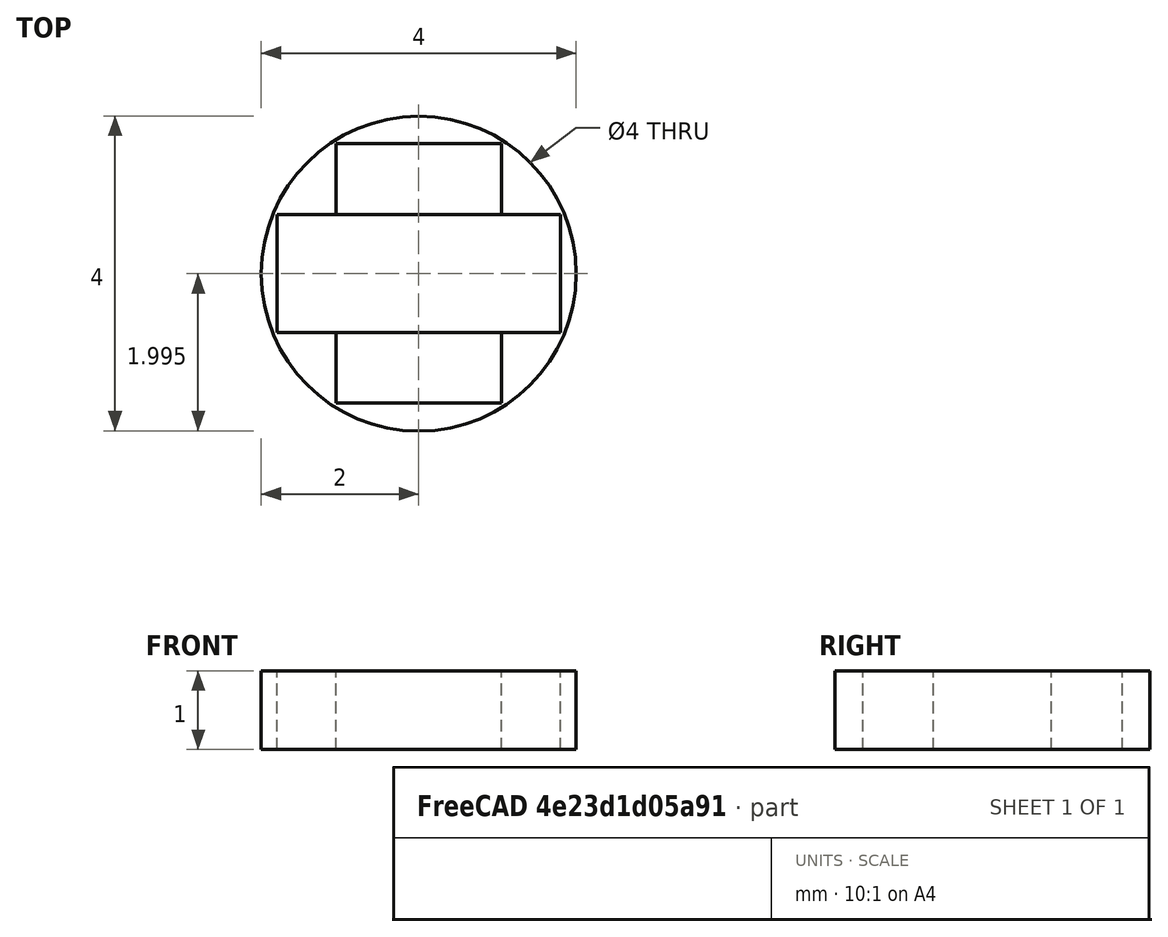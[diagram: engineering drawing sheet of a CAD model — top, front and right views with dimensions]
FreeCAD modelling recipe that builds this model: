
FCSTD DOCUMENT  (FreeCAD 0.17R13541 (Git))
Label: NOSE-PLANE
License: All rights reserved
LicenseURL: http://en.wikipedia.org/wiki/All_rights_reserved
objects: Drawing::FeatureViewPython×7, Part::Extrusion×2, Sketcher::SketchObject×1, Part::Feature×1, Drawing::FeatureViewPart×1, Drawing::FeaturePage×1
note: 4 computed .brp shape members not serialized (recipe doc carries the construction recipe); baked Part::Feature solids carry a one-line shape summary decoded from their .brp

FEATURE [Sketcher::SketchObject] Sketch
  sketch-geometry (11):
    g0: LineSegment StartX=-1.8 StartY=0.75 StartZ=0 EndX=1.8 EndY=0.75 EndZ=0
    g1: LineSegment StartX=1.8 StartY=0.75 StartZ=0 EndX=1.8 EndY=-0.75 EndZ=0
    g2: LineSegment StartX=1.8 StartY=-0.75 StartZ=0 EndX=-1.8 EndY=-0.75 EndZ=0
    g3: LineSegment StartX=-1.8 StartY=-0.75 StartZ=0 EndX=-1.8 EndY=0.75 EndZ=0
    g4: LineSegment StartX=-1.05 StartY=0.75 StartZ=0 EndX=-1.05 EndY=1.65 EndZ=0
    g5: LineSegment StartX=-1.05 StartY=1.65 StartZ=0 EndX=1.05 EndY=1.65 EndZ=0
    g6: LineSegment StartX=1.05 StartY=1.65 StartZ=0 EndX=1.05 EndY=0.75 EndZ=0
    g7: Circle CenterX=0.000107 CenterY=-0.004869 CenterZ=0 NormalX=0 NormalY=0 NormalZ=1 AngleXU=0 Radius=2
    g8: LineSegment StartX=-1.05 StartY=-0.75 StartZ=0 EndX=-1.05 EndY=-1.65 EndZ=0
    g9: LineSegment StartX=-1.05 StartY=-1.65 StartZ=0 EndX=1.05 EndY=-1.65 EndZ=0
    g10: LineSegment StartX=1.05 StartY=-1.65 StartZ=0 EndX=1.05 EndY=-0.75 EndZ=0
  constraints (33):
    c: Horizontal(g0)
    c: Coincident(g1,g0)
    c: Vertical(g1)
    c: Coincident(g2,g1)
    c: Horizontal(g2)
    c: Coincident(g3,g2)
    c: Coincident(g3,g0)
    c: Vertical(g3)
    c: Distance(g0) = 3.6
    c: Distance(g1) = 1.5
    c: Symmetric(g0,g0,g-2)
    c: Symmetric(g0,g1,g-1)
    c: PointOnObject(g4,g0)
    c: Vertical(g4)
    c: Coincident(g5,g4)
    c: Horizontal(g5)
    c: Coincident(g6,g5)
    c: PointOnObject(g6,g0)
    c: Vertical(g6)
    c: Distance(g5) = 2.1
    c: Symmetric(g4,g5,g-2)
    c: Distance(g6) = 0.9
    c: PointOnObject(g8,g2)
    c: Vertical(g8)
    c: Coincident(g9,g8)
    c: Horizontal(g9)
    c: Coincident(g10,g9)
    c: PointOnObject(g10,g2)
    c: Vertical(g10)
    c: Distance(g9) = 2.1
    c: Distance(g10) = 0.9
    c: Symmetric(g9,g8,g-2)
    c: Radius(g7) = 2
FEATURE [Part::Extrusion] Extrude
  Base = -> Sketch
  Dir = (0,0,1)
  DirMode = 2
  FaceMakerClass = Part::FaceMakerBullseye
  LengthFwd = 1
  LengthRev = 0
  Solid = false
  Symmetric = false
FEATURE [Part::Extrusion] Extrude001
  Base = -> Sketch
  Dir = (0,0,1)
  DirMode = 2
  FaceMakerClass = Part::FaceMakerBullseye
  LengthFwd = 1
  LengthRev = 0
  Solid = false
  Symmetric = false
FEATURE [Part::Feature] Extrude_cs
  shape: bbox 4.1 x 4.1 x 3e-07 mm, 0 faces, 0 solids (baked)
FEATURE [Drawing::FeatureViewPart] Ortho  label="Ortho_0_0"
  Direction = (0,0,1)
  HiddenWidth = 0.15
  LineWidth = 0.35
  Rotation = 0
  Scale = 30
  ShowHiddenLines = false
  ShowSmoothLines = false
  Source = -> Extrude_cs
  Tolerance = 0.05
  ViewResult = <g id="Ortho_0_0"\n   transform="rotate(0,148.497,85.8539) translate(148.497,85.8539) scale(30,30)"\n  >\n<g   fill="none"\n   stroke="rgb(0, 0, 0)"\n   stroke-linecap="butt"\n   stroke-linejoin="miter"\n   stroke-width="0.011667"\n   transform="scale(1,-1)"\n  >\n<path id= "1" d=" M -1.85 0.75 L 1.85 0.75 " />\n<path id= "2" d=" M 1.85 0.75 L 1.85 -0.75 " />\n<path id= "3" d=" M 1.85 -0.75 L -1.85 -0.75 " />\n<path id= "4" d=" M -1.85 -0.75 L -1.85 0.75 " />\n<path id= "5" d=" M -1.05 0.75 L -1.05 1.75 " />\n<path id= "6" d=" M -1.05 1.75 L 1.05 1.75 " />\n<path id= "7" d=" M 1.05 1.75 L 1.05 0.75 " />\n<circle cx ="0.000107" cy ="-0.004869" r ="2.05" /><path id= "9" d=" M -1.05 -0.75 L -1.05 -1.75 " />\n<path id= "10" d=" M -1.05 -1.75 L 1.05 -1.75 " />\n<path id= "11" d=" M 1.05 -1.75 L 1.05 -0.75 " />\n</g>\n</g>
  Visible = true
  X = 148.497
  Y = 85.8539
FEATURE [Drawing::FeatureViewPython] dia001  # drawing view (typed FeaturePython)
  Rotation = 0
  ViewResult = <g>  <circle cx ="148.500210" cy ="85.999970" r="0.250000" stroke="none" fill="rgb(255,0,0)" /> \n<line x1="83.284243" y1="166.821629" x2="187.120336" y2="38.138337" style="stroke:rgb(255,0,0);stroke-width:0.10" />\n<polygon points="109.880084,133.861603 111.525142,132.619112 111.450008,131.916008 110.746904,131.991142" style="fill:rgb(255,0,0);stroke:rgb(255,0,0);stroke-width:0" />\n<polygon points="187.120336,38.138337 185.475278,39.380828 185.550412,40.083932 186.253516,40.008798" style="fill:rgb(255,0,0);stroke:rgb(255,0,0);stroke-width:0" />\n<line x1="83.284243" y1="166.821629" x2="62.020181" y2="166.821629" style="stroke:rgb(255,0,0);stroke-width:0.10" />\n<text x="72.652212" y="164.821629" font-family="inherit" font-size="3.6" fill="rgb(0,0,0)" text-anchor="middle" transform="rotate(0.000000 72.652212,164.821629)" >Ø4.1</text> </g>
  Visible = true
  X = 0
  Y = 0
  arrowL1 = 2
  arrowL2 = 0.5
  arrowW = 1
  arrow_scheme = 0
  autoPlaceOffset = 2
  autoPlaceText = true
  centerPointDia = 0.5
  click1_x = 83.2842
  click1_y = 166.822
  click2_x = 62.0202
  click2_y = 168.594
  click3_x = 62.0202
  click3_y = 168.594
  comma_decimal_place = false
  lineColor = rgb(255,0,0)
  strokeWidth = 0.1
  textFormat_circular = Ø%(value)3.3f
  textRenderer_color = rgb(0,0,0)
  textRenderer_family = inherit
  textRenderer_size = 3.6
  unit_custom_scale = 1
  unit_scheme = 0
FEATURE [Drawing::FeatureViewPython] dim001  # drawing view (typed FeaturePython)
  Rotation = 0
  ViewResult = <g> \n  <line x1="116.997000" y1="33.353900" x2="116.997000" y2="17.732626" style="stroke:rgb(255,0,0);stroke-width:0.10" />\n<line x1="179.997000" y1="33.353900" x2="179.997000" y2="17.732626" style="stroke:rgb(255,0,0);stroke-width:0.10" />\n<line x1="116.997000" y1="18.732626" x2="179.997000" y2="18.732626" style="stroke:rgb(255,0,0);stroke-width:0.10" /> \n  <polygon points="179.997000,18.732626 177.997000,18.232626 177.497000,18.732626 177.997000,19.232626" style="fill:rgb(255,0,0);stroke:rgb(255,0,0);stroke-width:0" /><polygon points="116.997000,18.732626 118.997000,19.232626 119.497000,18.732626 118.997000,18.232626" style="fill:rgb(255,0,0);stroke:rgb(255,0,0);stroke-width:0" /> \n  <text x="148.497000" y="16.732626" font-family="inherit" font-size="3.6" fill="rgb(0,0,0)" text-anchor="middle" transform="rotate(0.000000 148.497000,16.732626)" >2.1</text> </g>
  Visible = true
  X = 0
  Y = 0
  arrowL1 = 2
  arrowL2 = 0.5
  arrowW = 1
  arrow_scheme = 0
  autoPlaceOffset = 2
  autoPlaceText = true
  click1_x = 141.001
  click1_y = 18.7326
  click2_x = 141.001
  click2_y = 18.7326
  comma_decimal_place = false
  dimension_line_overshoot = 1
  gap_datum_points = 0
  halfDimension_linear = false
  lineColor = rgb(255,0,0)
  strokeWidth = 0.1
  textFormat_linear = %(value)3.3f
  textRenderer_color = rgb(0,0,0)
  textRenderer_family = inherit
  textRenderer_size = 3.6
  unit_custom_scale = 0.8
  unit_scheme = 0
FEATURE [Drawing::FeatureViewPython] dim002  # drawing view (typed FeaturePython)
  Rotation = 0
  ViewResult = <g> \n  <line x1="179.997000" y1="33.353900" x2="226.550944" y2="33.353900" style="stroke:rgb(255,0,0);stroke-width:0.10" />\n<line x1="179.997000" y1="63.353900" x2="226.550944" y2="63.353900" style="stroke:rgb(255,0,0);stroke-width:0.10" />\n<line x1="225.550944" y1="33.353900" x2="225.550944" y2="63.353900" style="stroke:rgb(255,0,0);stroke-width:0.10" /> \n  <polygon points="225.550944,63.353900 226.050944,61.353900 225.550944,60.853900 225.050944,61.353900" style="fill:rgb(255,0,0);stroke:rgb(255,0,0);stroke-width:0" /><polygon points="225.550944,33.353900 225.050944,35.353900 225.550944,35.853900 226.050944,35.353900" style="fill:rgb(255,0,0);stroke:rgb(255,0,0);stroke-width:0" /> \n  <text x="223.550944" y="48.353900" font-family="inherit" font-size="3.6" fill="rgb(0,0,0)" text-anchor="middle" transform="rotate(-90.000000 223.550944,48.353900)" >1</text> </g>
  Visible = true
  X = 0
  Y = 0
  arrowL1 = 2
  arrowL2 = 0.5
  arrowW = 1
  arrow_scheme = 0
  autoPlaceOffset = 2
  autoPlaceText = true
  click1_x = 225.551
  click1_y = 53.4133
  click2_x = 225.551
  click2_y = 53.4133
  comma_decimal_place = false
  dimension_line_overshoot = 1
  gap_datum_points = 0
  halfDimension_linear = false
  lineColor = rgb(255,0,0)
  strokeWidth = 0.1
  textFormat_linear = %(value)3.3f
  textRenderer_color = rgb(0,0,0)
  textRenderer_family = inherit
  textRenderer_size = 3.6
  unit_custom_scale = 0.8
  unit_scheme = 0
FEATURE [Drawing::FeatureViewPython] dim003  # drawing view (typed FeaturePython)
  Rotation = 0
  ViewResult = <g> \n  <line x1="203.997000" y1="63.353900" x2="226.550944" y2="63.353900" style="stroke:rgb(255,0,0);stroke-width:0.10" />\n<line x1="203.997000" y1="108.353900" x2="226.550944" y2="108.353900" style="stroke:rgb(255,0,0);stroke-width:0.10" />\n<line x1="225.550944" y1="63.353900" x2="225.550944" y2="108.353900" style="stroke:rgb(255,0,0);stroke-width:0.10" /> \n  <polygon points="225.550944,108.353900 226.050944,106.353900 225.550944,105.853900 225.050944,106.353900" style="fill:rgb(255,0,0);stroke:rgb(255,0,0);stroke-width:0" /><polygon points="225.550944,63.353900 225.050944,65.353900 225.550944,65.853900 226.050944,65.353900" style="fill:rgb(255,0,0);stroke:rgb(255,0,0);stroke-width:0" /> \n  <text x="223.550944" y="85.853900" font-family="inherit" font-size="3.6" fill="rgb(0,0,0)" text-anchor="middle" transform="rotate(-90.000000 223.550944,85.853900)" >1.5</text> </g>
  Visible = true
  X = 0
  Y = 0
  arrowL1 = 2
  arrowL2 = 0.5
  arrowW = 1
  arrow_scheme = 0
  autoPlaceOffset = 2
  autoPlaceText = true
  click1_x = 225.551
  click1_y = 84.55
  click2_x = 225.551
  click2_y = 84.55
  comma_decimal_place = false
  dimension_line_overshoot = 1
  gap_datum_points = 0
  halfDimension_linear = false
  lineColor = rgb(255,0,0)
  strokeWidth = 0.1
  textFormat_linear = %(value)3.3f
  textRenderer_color = rgb(0,0,0)
  textRenderer_family = inherit
  textRenderer_size = 3.6
  unit_custom_scale = 0.8
  unit_scheme = 0
FEATURE [Drawing::FeatureViewPython] dim004  # drawing view (typed FeaturePython)
  Rotation = 0
  ViewResult = <g> \n  <line x1="179.997000" y1="138.353900" x2="226.550944" y2="138.353900" style="stroke:rgb(255,0,0);stroke-width:0.10" />\n<line x1="179.997000" y1="108.353900" x2="226.550944" y2="108.353900" style="stroke:rgb(255,0,0);stroke-width:0.10" />\n<line x1="225.550944" y1="138.353900" x2="225.550944" y2="108.353900" style="stroke:rgb(255,0,0);stroke-width:0.10" /> \n  <polygon points="225.550944,108.353900 225.050944,110.353900 225.550944,110.853900 226.050944,110.353900" style="fill:rgb(255,0,0);stroke:rgb(255,0,0);stroke-width:0" /><polygon points="225.550944,138.353900 226.050944,136.353900 225.550944,135.853900 225.050944,136.353900" style="fill:rgb(255,0,0);stroke:rgb(255,0,0);stroke-width:0" /> \n  <text x="223.550944" y="123.353900" font-family="inherit" font-size="3.6" fill="rgb(0,0,0)" text-anchor="middle" transform="rotate(-90.000000 223.550944,123.353900)" >1</text> </g>
  Visible = true
  X = 0
  Y = 0
  arrowL1 = 2
  arrowL2 = 0.5
  arrowW = 1
  arrow_scheme = 0
  autoPlaceOffset = 2
  autoPlaceText = true
  click1_x = 225.551
  click1_y = 124.294
  click2_x = 225.551
  click2_y = 124.294
  comma_decimal_place = false
  dimension_line_overshoot = 1
  gap_datum_points = 0
  halfDimension_linear = false
  lineColor = rgb(255,0,0)
  strokeWidth = 0.1
  textFormat_linear = %(value)3.3f
  textRenderer_color = rgb(0,0,0)
  textRenderer_family = inherit
  textRenderer_size = 3.6
  unit_custom_scale = 0.8
  unit_scheme = 0
FEATURE [Drawing::FeatureViewPython] dim005  # drawing view (typed FeaturePython)
  Rotation = 0
  ViewResult = <g> \n  <line x1="116.997000" y1="138.353900" x2="116.997000" y2="130.887813" style="stroke:rgb(255,0,0);stroke-width:0.10" />\n<line x1="179.997000" y1="138.353900" x2="179.997000" y2="130.887813" style="stroke:rgb(255,0,0);stroke-width:0.10" />\n<line x1="116.997000" y1="131.887813" x2="179.997000" y2="131.887813" style="stroke:rgb(255,0,0);stroke-width:0.10" /> \n  <polygon points="179.997000,131.887813 177.997000,131.387813 177.497000,131.887813 177.997000,132.387813" style="fill:rgb(255,0,0);stroke:rgb(255,0,0);stroke-width:0" /><polygon points="116.997000,131.887813 118.997000,132.387813 119.497000,131.887813 118.997000,131.387813" style="fill:rgb(255,0,0);stroke:rgb(255,0,0);stroke-width:0" /> \n  <text x="148.497000" y="129.887813" font-family="inherit" font-size="3.6" fill="rgb(0,0,0)" text-anchor="middle" transform="rotate(0.000000 148.497000,129.887813)" >2.1</text> </g>
  Visible = true
  X = 0
  Y = 0
  arrowL1 = 2
  arrowL2 = 0.5
  arrowW = 1
  arrow_scheme = 0
  autoPlaceOffset = 2
  autoPlaceText = true
  click1_x = 167.075
  click1_y = 131.888
  click2_x = 167.075
  click2_y = 131.888
  comma_decimal_place = false
  dimension_line_overshoot = 1
  gap_datum_points = 0
  halfDimension_linear = false
  lineColor = rgb(255,0,0)
  strokeWidth = 0.1
  textFormat_linear = %(value)3.3f
  textRenderer_color = rgb(0,0,0)
  textRenderer_family = inherit
  textRenderer_size = 3.6
  unit_custom_scale = 0.8
  unit_scheme = 0
FEATURE [Drawing::FeatureViewPython] dim006  # drawing view (typed FeaturePython)
  Rotation = 0
  ViewResult = <g> \n  <line x1="203.997000" y1="108.353900" x2="203.997000" y2="158.455316" style="stroke:rgb(255,0,0);stroke-width:0.10" />\n<line x1="92.997000" y1="108.353900" x2="92.997000" y2="158.455316" style="stroke:rgb(255,0,0);stroke-width:0.10" />\n<line x1="203.997000" y1="157.455316" x2="92.997000" y2="157.455316" style="stroke:rgb(255,0,0);stroke-width:0.10" /> \n  <polygon points="92.997000,157.455316 94.997000,157.955316 95.497000,157.455316 94.997000,156.955316" style="fill:rgb(255,0,0);stroke:rgb(255,0,0);stroke-width:0" /><polygon points="203.997000,157.455316 201.997000,156.955316 201.497000,157.455316 201.997000,157.955316" style="fill:rgb(255,0,0);stroke:rgb(255,0,0);stroke-width:0" /> \n  <text x="148.497000" y="155.455316" font-family="inherit" font-size="3.6" fill="rgb(0,0,0)" text-anchor="middle" transform="rotate(0.000000 148.497000,155.455316)" >3.7</text> </g>
  Visible = true
  X = 0
  Y = 0
  arrowL1 = 2
  arrowL2 = 0.5
  arrowW = 1
  arrow_scheme = 0
  autoPlaceOffset = 2
  autoPlaceText = true
  click1_x = 170.872
  click1_y = 157.455
  click2_x = 170.872
  click2_y = 157.455
  comma_decimal_place = false
  dimension_line_overshoot = 1
  gap_datum_points = 0
  halfDimension_linear = false
  lineColor = rgb(255,0,0)
  strokeWidth = 0.1
  textFormat_linear = %(value)3.3f
  textRenderer_color = rgb(0,0,0)
  textRenderer_family = inherit
  textRenderer_size = 3.6
  unit_custom_scale = 0.8
  unit_scheme = 0
FEATURE [Drawing::FeaturePage] Page
  EditableTexts = AUTHOR NAME | DRAWING TITLE | FreeCAD DRAWING | A4 | X / Y | SCALE | PN | DN | DD/MM/YYYY | REV A
  Group = -> [Ortho,dia001,dim001,dim002,dim003,dim004,dim005,dim006]
  Template = <path>
note: 1 file-system path scrubbed to <path> (originals preserved in the JSON sidecar)
